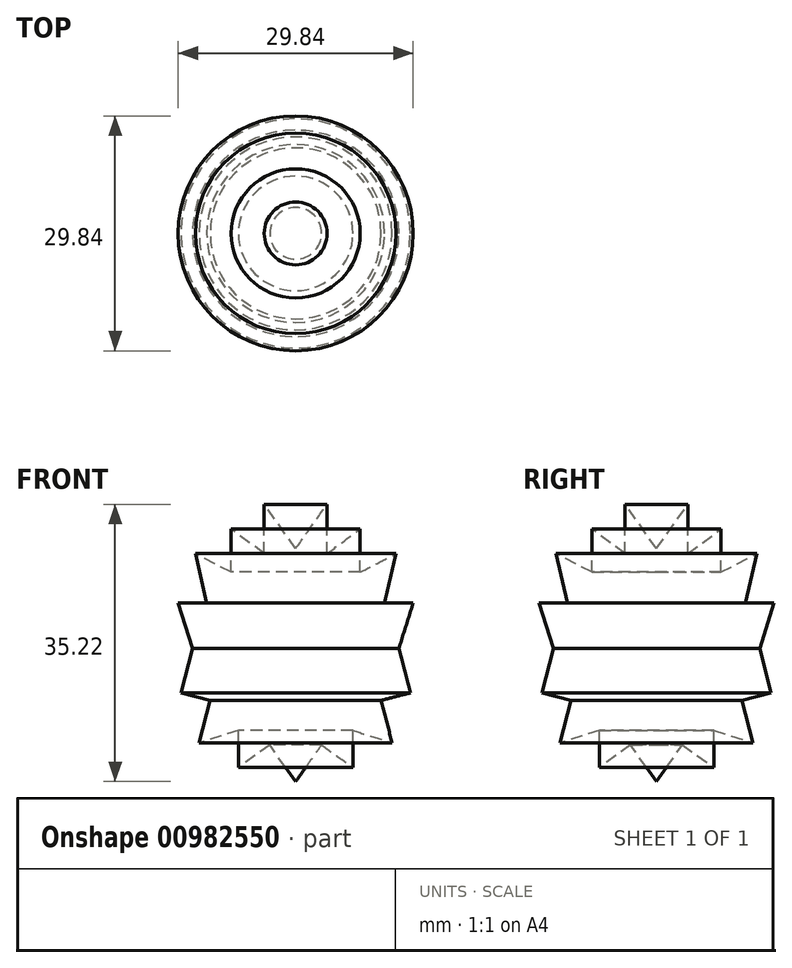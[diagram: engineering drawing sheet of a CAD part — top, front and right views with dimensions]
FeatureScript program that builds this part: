
annotation { "Feature Type Name" : "Feature", "Feature Type Description" : "" }
export const myFeature = defineFeature(function(context is Context, id is Id, definition is map)
    precondition{}
    {
        {
            var Q0;
            Q0=qCreatedBy(makeId("Front.planeOp"),FACE);
            var sketch = newSketch(context, id + "F0", { "sketchPlane" : qUnion([Q0])});
            skCircle(sketch, "E0", {"center": v(0, 0) * mm, "radius": 12.7 * mm});
            skLineSegment(sketch, "E1", {"start": v(0, 12.7) * mm, "end": v(0, 0) * mm});
            skLineSegment(sketch, "E2", {"start": v(0, 0) * mm, "end": v(0, -12.7) * mm});
            skLineSegment(sketch, "E3", {"start": v(0, 12.7) * mm, "end": v(-4, 18.32) * mm});
            skLineSegment(sketch, "E4", {"start": v(-4, 18.32) * mm, "end": v(-4, 12.06) * mm});
            skLineSegment(sketch, "E5", {"start": v(-4, 12.06) * mm, "end": v(-8.2, 15.19) * mm});
            skPoint(sketch, "E5.endSnap0", {"position": v(-4, 15.19) * mm});
            skLineSegment(sketch, "E6", {"start": v(-8.2, 15.19) * mm, "end": v(-8.2, 9.7) * mm});
            skLineSegment(sketch, "E7", {"start": v(-8.2, 9.7) * mm, "end": v(-12.75, 12.06) * mm});
            skLineSegment(sketch, "E8", {"start": v(-12.75, 12.06) * mm, "end": v(-11.3, 5.8) * mm});
            skLineSegment(sketch, "E9", {"start": v(-11.3, 5.8) * mm, "end": v(-14.92, 5.8) * mm});
            skLineSegment(sketch, "E10", {"start": v(-14.92, 5.8) * mm, "end": v(-13.11, 0) * mm});
            skPoint(sketch, "E10.endSnap0", {"position": v(-13.11, 5.8) * mm});
            skLineSegment(sketch, "E11", {"start": v(-13.11, 0) * mm, "end": v(-14.56, -5.63) * mm});
            skLineSegment(sketch, "E12", {"start": v(-14.56, -5.63) * mm, "end": v(-10.86, -6.58) * mm});
            skLineSegment(sketch, "E13", {"start": v(-10.86, -6.58) * mm, "end": v(-12.25, -11.99) * mm});
            skLineSegment(sketch, "E14", {"start": v(-12.25, -11.99) * mm, "end": v(-7.28, -10.4) * mm});
            skLineSegment(sketch, "E15", {"start": v(-7.28, -10.4) * mm, "end": v(-7.28, -15.1) * mm});
            skLineSegment(sketch, "E16", {"start": v(-7.28, -15.1) * mm, "end": v(-3.29, -12.27) * mm});
            skLineSegment(sketch, "E17", {"start": v(-3.29, -12.27) * mm, "end": v(0, -16.9) * mm});
            skLineSegment(sketch, "E18", {"start": v(0, -16.9) * mm, "end": v(0, -12.7) * mm});
            skSolve(sketch);
        }
        {
            var Q0;
            {var subQ2=sQuery(id+"F0.wireOp",EDGE,"E17");Q0=makeQuery(id+"F0.imprint","IMPRINT",FACE,{"disambiguationData":[TD([[makeQuery(id+"F0.imprint","IMPRINT",EDGE,{"derivedFrom":subQ2}),1.0]])]});}
            var Q1;
            {var subQ0=sQuery(id+"F0.wireOp",EDGE,"E15");Q1=makeQuery(id+"F0.imprint","IMPRINT",FACE,{"disambiguationData":[TD([[makeQuery(id+"F0.imprint","IMPRINT",EDGE,{"derivedFrom":subQ0}),1.0]])]});}
            var Q2;
            {var subQ0=sQuery(id+"F0.wireOp",EDGE,"E13");Q2=makeQuery(id+"F0.imprint","IMPRINT",FACE,{"disambiguationData":[TD([[makeQuery(id+"F0.imprint","IMPRINT",EDGE,{"derivedFrom":subQ0}),1.0]])]});}
            var Q3;
            {var subQ5=sQuery(id+"F0.wireOp",EDGE,"E1");Q3=makeQuery(id+"F0.imprint","IMPRINT",FACE,{"disambiguationData":[TD([[makeQuery(id+"F0.imprint","IMPRINT",EDGE,{"derivedFrom":subQ5}),-1.0]])]});}
            var Q4;
            {var subQ0=sQuery(id+"F0.wireOp",EDGE,"E9");Q4=makeQuery(id+"F0.imprint","IMPRINT",FACE,{"disambiguationData":[TD([[makeQuery(id+"F0.imprint","IMPRINT",EDGE,{"derivedFrom":subQ0}),1.0]])]});}
            var Q5;
            {var subQ0=sQuery(id+"F0.wireOp",EDGE,"E7");Q5=makeQuery(id+"F0.imprint","IMPRINT",FACE,{"disambiguationData":[TD([[makeQuery(id+"F0.imprint","IMPRINT",EDGE,{"derivedFrom":subQ0}),1.0]])]});}
            var Q6;
            {var subQ0=sQuery(id+"F0.wireOp",EDGE,"E5");Q6=makeQuery(id+"F0.imprint","IMPRINT",FACE,{"disambiguationData":[TD([[makeQuery(id+"F0.imprint","IMPRINT",EDGE,{"derivedFrom":subQ0}),1.0]])]});}
            var Q7;
            {var subQ0=sQuery(id+"F0.wireOp",EDGE,"E3");Q7=makeQuery(id+"F0.imprint","IMPRINT",FACE,{"disambiguationData":[TD([[makeQuery(id+"F0.imprint","IMPRINT",EDGE,{"derivedFrom":subQ0}),1.0]])]});}
            var Q8;
            Q8=sQuery(id+"F0.wireOp",EDGE,"E2");
            revolve(context, id + "F1", {"surfaceOperationType" : NewSurfaceOperationType.NEW, "entities" : qUnion([Q0, Q1, Q2, Q3, Q4, Q5, Q6, Q7]), "axis" : qUnion([Q8]), "revolveType" : RevolveType.FULL});
        }
    });
